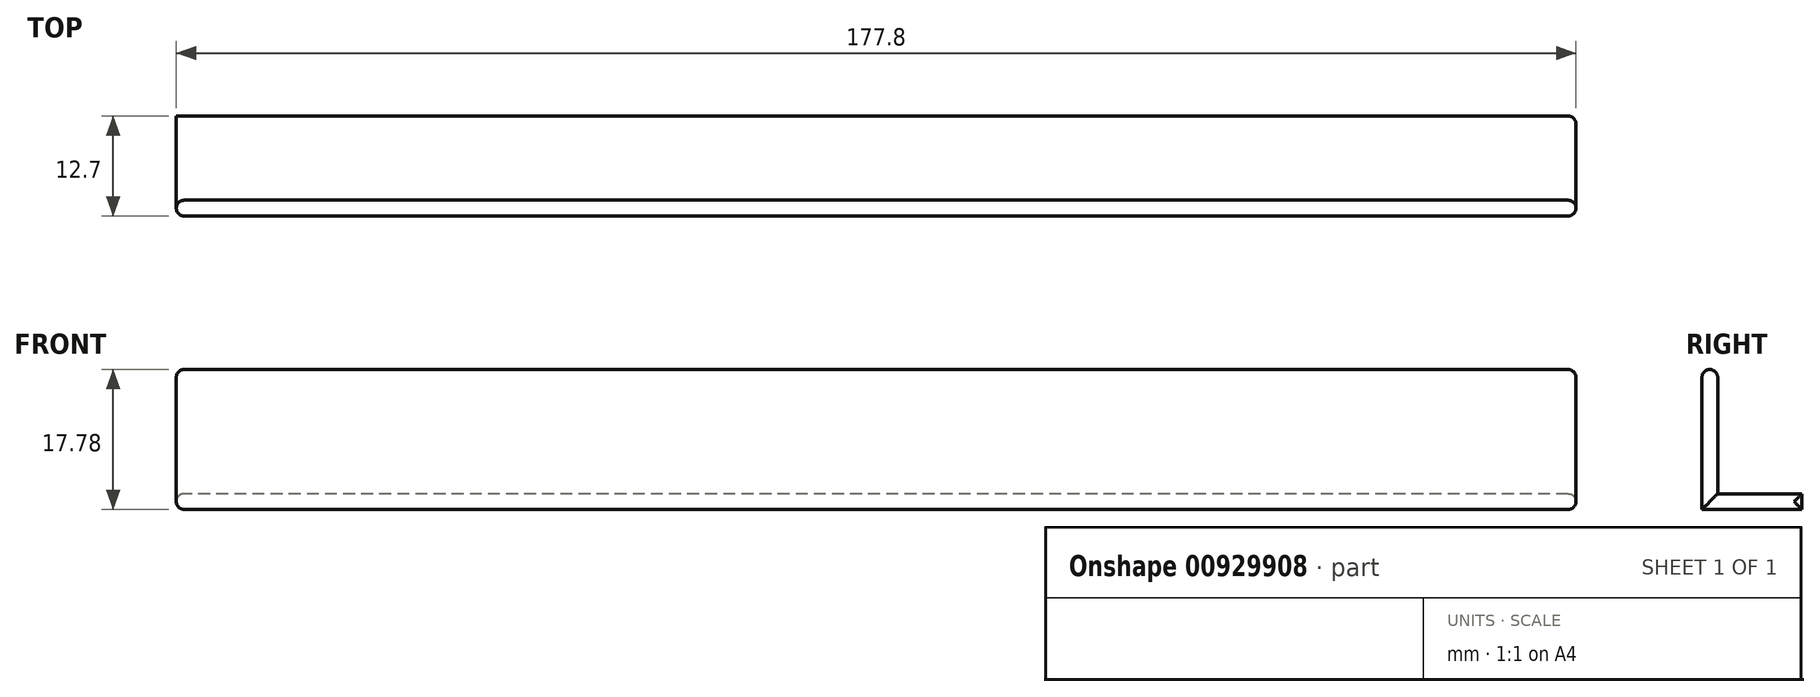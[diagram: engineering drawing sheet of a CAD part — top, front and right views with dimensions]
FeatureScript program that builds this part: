
annotation { "Feature Type Name" : "Feature", "Feature Type Description" : "" }
export const myFeature = defineFeature(function(context is Context, id is Id, definition is map)
    precondition{}
    {
        {
            var Q0;
            Q0=qCreatedBy(makeId("Right.planeOp"),FACE);
            var sketch = newSketch(context, id + "F0", { "sketchPlane" : qUnion([Q0])});
            skLineSegment(sketch, "E0", {"start": v(0, 0) * mm, "end": v(0, 17.78) * mm});
            skLineSegment(sketch, "E1", {"start": v(0, 0) * mm, "end": v(12.7, 0) * mm});
            skLineSegment(sketch, "E2", {"start": v(0, 17.78) * mm, "end": v(2, 17.78) * mm});
            skLineSegment(sketch, "E3", {"start": v(2, 17.78) * mm, "end": v(2, 2) * mm});
            skLineSegment(sketch, "E4", {"start": v(2, 2) * mm, "end": v(12.7, 2) * mm});
            skLineSegment(sketch, "E5", {"start": v(12.7, 2) * mm, "end": v(12.7, 0) * mm});
            skSolve(sketch);
        }
        {
            var Q0;
            Q0 = qSketchRegion(id + "F0", true);
            extrude(context, id + "F1", {"entities" : qUnion([Q0]), "endBound" : BoundingType.SYMMETRIC, "depth" : 177.8 * mm, "offsetDistance" : 25.4 * mm});
        }
        {
            var Q0;
            Q0=makeQuery(id+"F1.opExtrude","SWEPT_EDGE",EDGE,{"disambiguationData":[OSD([sQuery(id+"F0.wireOp",EDGE,"E0"),sQuery(id+"F0.wireOp",EDGE,"E2")])]});
            var Q1;
            Q1=makeQuery(id+"F1.opExtrude","CAP_EDGE",EDGE,{"disambiguationData":[OSD([sQuery(id+"F0.wireOp",EDGE,"E0")])],"isStart":false});
            var Q2;
            Q2=makeQuery(id+"F1.opExtrude","SWEPT_FACE",FACE,{"disambiguationData":[OSD([sQuery(id+"F0.wireOp",EDGE,"E2")])]});
            var Q3;
            Q3=makeQuery(id+"F1.opExtrude","CAP_EDGE",EDGE,{"disambiguationData":[OSD([sQuery(id+"F0.wireOp",EDGE,"E2")])],"isStart":false});
            var Q4;
            Q4=makeQuery(id+"F1.opExtrude","CAP_EDGE",EDGE,{"disambiguationData":[OSD([sQuery(id+"F0.wireOp",EDGE,"E3")])],"isStart":false});
            var Q5;
            Q5=makeQuery(id+"F1.opExtrude","CAP_FACE",FACE,{"disambiguationData":[OSD([sQuery(id+"F0.wireOp",EDGE,"E0"),sQuery(id+"F0.wireOp",EDGE,"E1"),sQuery(id+"F0.wireOp",EDGE,"E2"),sQuery(id+"F0.wireOp",EDGE,"E3"),sQuery(id+"F0.wireOp",EDGE,"E4"),sQuery(id+"F0.wireOp",EDGE,"E5")])],"isStart":false});
            var Q6;
            Q6=makeQuery(id+"F1.opExtrude","CAP_EDGE",EDGE,{"disambiguationData":[OSD([sQuery(id+"F0.wireOp",EDGE,"E0")])],"isStart":true});
            var Q7;
            Q7=makeQuery(id+"F1.opExtrude","CAP_EDGE",EDGE,{"disambiguationData":[OSD([sQuery(id+"F0.wireOp",EDGE,"E3")])],"isStart":true});
            var Q8;
            Q8=makeQuery(id+"F1.opExtrude","CAP_EDGE",EDGE,{"disambiguationData":[OSD([sQuery(id+"F0.wireOp",EDGE,"E4")])],"isStart":true});
            var Q9;
            Q9=makeQuery(id+"F1.opExtrude","CAP_EDGE",EDGE,{"disambiguationData":[OSD([sQuery(id+"F0.wireOp",EDGE,"E1")])],"isStart":true});
            fillet(context, id + "F2", {"entities" : qUnion([Q0, Q1, Q2, Q3, Q4, Q5, Q6, Q7, Q8, Q9]), "radius" : 1 * mm, "tangentPropagation" : true, "allowEdgeOverflow" : false});
        }
    });
